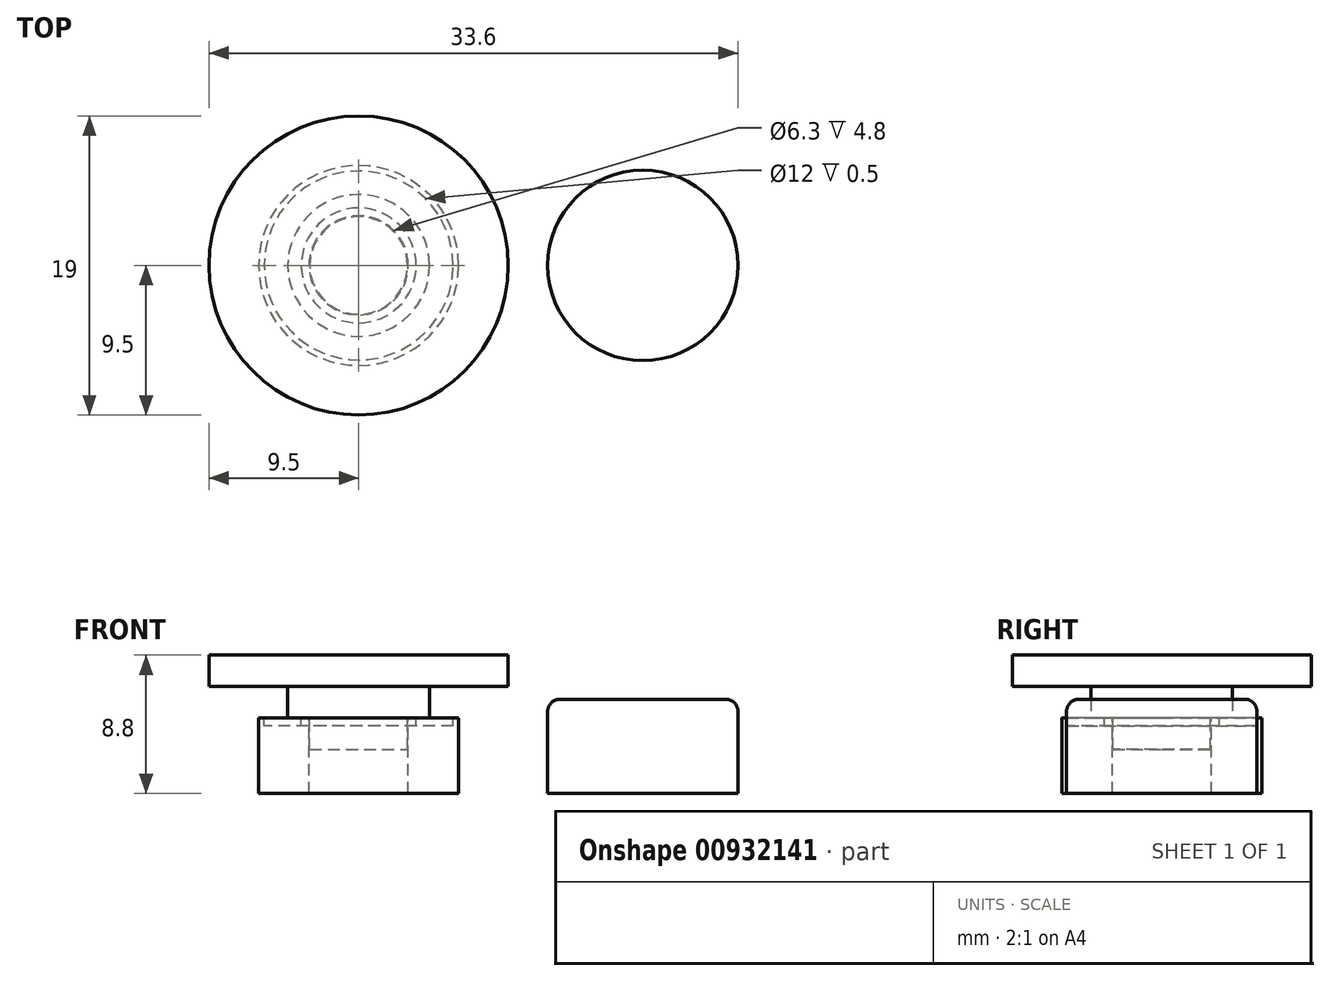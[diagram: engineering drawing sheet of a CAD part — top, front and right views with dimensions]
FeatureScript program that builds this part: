
annotation { "Feature Type Name" : "Feature", "Feature Type Description" : "" }
export const myFeature = defineFeature(function(context is Context, id is Id, definition is map)
    precondition{}
    {
        {
            var Q0;
            Q0=qCreatedBy(makeId("Top.planeOp"),FACE);
            var sketch = newSketch(context, id + "F0", { "sketchPlane" : qUnion([Q0])});
            skCircle(sketch, "E0", {"center": v(0, 0) * mm, "radius": 6.35 * mm});
            skSolve(sketch);
        }
        {
            var Q0;
            Q0=makeQuery(id+"F0.imprint","IMPRINT",FACE,{"disambiguationData":[TD([[makeQuery(id+"F0.imprint","IMPRINT",EDGE,{"derivedFrom":sQuery(id+"F0.wireOp",EDGE,"E0")}),1.0]])]});
            extrude(context, id + "F1", {"entities" : qUnion([Q0]), "depth" : 4.8 * mm, "offsetDistance" : 25 * mm});
        }
        {
            var Q0;
            Q0=makeQuery(id+"F1.opExtrude","CAP_FACE",FACE,{"disambiguationData":[OSD([sQuery(id+"F0.wireOp",EDGE,"E0")])],"isStart":false});
            var sketch = newSketch(context, id + "F2", { "sketchPlane" : qUnion([Q0])});
            skCircle(sketch, "E1", {"center": v(0, 0) * mm, "radius": 3.15 * mm});
            skSolve(sketch);
        }
        {
            var Q0;
            Q0=makeQuery(id+"F2.imprint","IMPRINT",FACE,{"disambiguationData":[TD([[makeQuery(id+"F2.imprint","IMPRINT",EDGE,{"derivedFrom":sQuery(id+"F2.wireOp",EDGE,"E1")}),1.0]])]});
            extrude(context, id + "F3", {"entities" : qUnion([Q0]), "operationType" : NewBodyOperationType.REMOVE, "endBound" : BoundingType.THROUGH_ALL, "oppositeDirection" : true, "depth" : 25 * mm, "offsetDistance" : 25 * mm});
        }
        {
            var Q0;
            Q0=qCreatedBy(makeId("Top.planeOp"),FACE);
            var sketch = newSketch(context, id + "F4", { "sketchPlane" : qUnion([Q0])});
            skLineSegment(sketch, "E2.bottom", {"start": v(22.5, 11.25) * mm, "end": v(-22.5, 11.25) * mm});
            skLineSegment(sketch, "E2.top", {"start": v(22.5, -11.25) * mm, "end": v(-22.5, -11.25) * mm});
            skLineSegment(sketch, "E2.left", {"start": v(27.5, 6.25) * mm, "end": v(27.5, -6.25) * mm});
            skLineSegment(sketch, "E2.right", {"start": v(-27.5, 6.25) * mm, "end": v(-27.5, -6.25) * mm});
            skPoint(sketch, "E2.middle", {"position": v(0, 0) * mm});
            skPoint(sketch, "E3.visualSharp", {"position": v(-27.5, 11.25) * mm});
            skArc(sketch, "E3.filletArc", {"start": v(-22.5, 11.25) * mm, "mid": v(-26.04, 9.79) * mm, "end": v(-27.5, 6.25) * mm});
            skPoint(sketch, "E4.visualSharp", {"position": v(-27.5, -11.25) * mm});
            skArc(sketch, "E4.filletArc", {"start": v(-27.5, -6.25) * mm, "mid": v(-26.04, -9.79) * mm, "end": v(-22.5, -11.25) * mm});
            skPoint(sketch, "E5.visualSharp", {"position": v(27.5, 11.25) * mm});
            skArc(sketch, "E5.filletArc", {"start": v(27.5, 6.25) * mm, "mid": v(26.04, 9.79) * mm, "end": v(22.5, 11.25) * mm});
            skPoint(sketch, "E6.visualSharp", {"position": v(27.5, -11.25) * mm});
            skArc(sketch, "E6.filletArc", {"start": v(22.5, -11.25) * mm, "mid": v(26.04, -9.79) * mm, "end": v(27.5, -6.25) * mm});
            skCircle(sketch, "E7", {"center": v(0, 0) * mm, "radius": 6.4 * mm});
            skSolve(sketch);
        }
        {
            var Q0;
            Q0=makeQuery(id+"F4.imprint","IMPRINT",FACE,{"disambiguationData":[TD([[makeQuery(id+"F4.imprint","IMPRINT",EDGE,{"derivedFrom":sQuery(id+"F4.wireOp",EDGE,"E2.bottom")}),1.0]])]});
            extrude(context, id + "F5", {"entities" : qUnion([Q0]), "depth" : 6 * mm, "offsetDistance" : 25 * mm});
        }
        {
            var Q0;
            Q0=makeQuery(id+"F1.opExtrude","CAP_FACE",FACE,{"disambiguationData":[OSD([sQuery(id+"F0.wireOp",EDGE,"E0")])],"isStart":false});
            var sketch = newSketch(context, id + "F6", { "sketchPlane" : qUnion([Q0])});
            skCircle(sketch, "E8", {"center": v(0, 0) * mm, "radius": 6 * mm});
            skCircle(sketch, "E9", {"center": v(0, 0) * mm, "radius": 3.65 * mm});
            skSolve(sketch);
        }
        {
            var Q0;
            Q0=makeQuery(id+"F6.imprint","IMPRINT",FACE,{"disambiguationData":[TD([[makeQuery(id+"F6.imprint","IMPRINT",EDGE,{"derivedFrom":sQuery(id+"F6.wireOp",EDGE,"E8")}),1.0]])]});
            extrude(context, id + "F7", {"entities" : qUnion([Q0]), "operationType" : NewBodyOperationType.REMOVE, "oppositeDirection" : true, "depth" : 0.5 * mm, "offsetDistance" : 25 * mm});
        }
        {
            var Q0;
            Q0=makeQuery(id+"F5.opExtrude","CAP_FACE",FACE,{"disambiguationData":[OSD([sQuery(id+"F4.wireOp",EDGE,"E2.bottom"),sQuery(id+"F4.wireOp",EDGE,"E2.top"),sQuery(id+"F4.wireOp",EDGE,"E2.left"),sQuery(id+"F4.wireOp",EDGE,"E2.right"),sQuery(id+"F4.wireOp",EDGE,"E3.filletArc"),sQuery(id+"F4.wireOp",EDGE,"E4.filletArc"),sQuery(id+"F4.wireOp",EDGE,"E5.filletArc"),sQuery(id+"F4.wireOp",EDGE,"E6.filletArc"),sQuery(id+"F4.wireOp",EDGE,"E7")])],"isStart":false});
            var sketch = newSketch(context, id + "F8", { "sketchPlane" : qUnion([Q0])});
            skLineSegment(sketch, "E10", {"start": v(0, 18.58) * mm, "end": v(0, -13.85) * mm, "construction": true});
            skCircle(sketch, "E11", {"center": v(-18.05, 0) * mm, "radius": 6.05 * mm});
            skCircle(sketch, "E12.MirrorC", {"center": v(18.05, 0) * mm, "radius": 6.05 * mm});
            skSolve(sketch);
        }
        {
            var Q0;
            Q0=makeQuery(id+"F8.imprint","IMPRINT",FACE,{"disambiguationData":[TD([[makeQuery(id+"F8.imprint","IMPRINT",EDGE,{"derivedFrom":sQuery(id+"F8.wireOp",EDGE,"E11")}),1.0]])]});
            var Q1;
            Q1=makeQuery(id+"F8.imprint","IMPRINT",FACE,{"disambiguationData":[TD([[makeQuery(id+"F8.imprint","IMPRINT",EDGE,{"derivedFrom":sQuery(id+"F8.wireOp",EDGE,"E12.MirrorC")}),-1.0]])]});
            extrude(context, id + "F9", {"entities" : qUnion([Q0, Q1]), "operationType" : NewBodyOperationType.REMOVE, "endBound" : BoundingType.THROUGH_ALL, "oppositeDirection" : true, "depth" : 25 * mm, "offsetDistance" : 25 * mm});
        }
        {
            var Q0;
            Q0=makeQuery(id+"F5.opExtrude","CAP_FACE",FACE,{"disambiguationData":[OSD([sQuery(id+"F4.wireOp",EDGE,"E2.bottom"),sQuery(id+"F4.wireOp",EDGE,"E2.top"),sQuery(id+"F4.wireOp",EDGE,"E2.left"),sQuery(id+"F4.wireOp",EDGE,"E2.right"),sQuery(id+"F4.wireOp",EDGE,"E3.filletArc"),sQuery(id+"F4.wireOp",EDGE,"E4.filletArc"),sQuery(id+"F4.wireOp",EDGE,"E5.filletArc"),sQuery(id+"F4.wireOp",EDGE,"E6.filletArc"),sQuery(id+"F4.wireOp",EDGE,"E7")])],"isStart":false});
            fillet(context, id + "F10", {"entities" : qUnion([Q0]), "radius" : 0.8 * mm, "tangentPropagation" : true, "allowEdgeOverflow" : false});
        }
        {
            var Q0;
            Q0=makeQuery(id+"F7.boolean.opBoolean","SPLIT",FACE,{"disambiguationData":[TD([makeQuery(id+"F3.boolean.opBoolean","COPY",FACE,{"derivedFrom":makeQuery(id+"F3.opExtrude","SWEPT_FACE",FACE,{"disambiguationData":[OSD([sQuery(id+"F2.wireOp",EDGE,"E1")])]})})])],"derivedFrom":makeQuery(id+"F1.opExtrude","CAP_FACE",FACE,{"disambiguationData":[OSD([sQuery(id+"F0.wireOp",EDGE,"E0")])],"isStart":false})});
            cPlane(context, id + "F11", {"entities" : qUnion([Q0]), "cplaneType" : CPlaneType.OFFSET, "offset" : 0 * mm, "width" : 150 * mm, "height" : 150 * mm});
        }
        {
            var Q0;
            Q0=qCreatedBy(id+"F11.planeOp",FACE);
            var sketch = newSketch(context, id + "F12", { "sketchPlane" : qUnion([Q0])});
            skCircle(sketch, "E13", {"center": v(0, 0) * mm, "radius": 4.5 * mm});
            skSolve(sketch);
        }
        {
            var Q0;
            Q0 = qSketchRegion(id + "F12", true);
            extrude(context, id + "F13", {"entities" : qUnion([Q0]), "depth" : 2 * mm, "offsetDistance" : 25 * mm});
        }
        {
            var Q0;
            Q0=makeQuery(id+"F13.opExtrude","CAP_FACE",FACE,{"disambiguationData":[OSD([sQuery(id+"F12.wireOp",EDGE,"E13")])],"isStart":false});
            var sketch = newSketch(context, id + "F14", { "sketchPlane" : qUnion([Q0])});
            skCircle(sketch, "E14", {"center": v(0, 0) * mm, "radius": 9.5 * mm});
            skSolve(sketch);
        }
        {
            var Q0;
            Q0=makeQuery(id+"F14.imprint","IMPRINT",FACE,{"disambiguationData":[TD([[makeQuery(id+"F14.imprint","IMPRINT",EDGE,{"derivedFrom":makeQuery(id+"F13.opExtrude","CAP_EDGE",EDGE,{"disambiguationData":[OSD([sQuery(id+"F12.wireOp",EDGE,"E13")])],"isStart":false})}),1.0]])]});
            var Q1;
            Q1=makeQuery(id+"F14.imprint","IMPRINT",FACE,{"disambiguationData":[TD([[makeQuery(id+"F14.imprint","IMPRINT",EDGE,{"derivedFrom":sQuery(id+"F14.wireOp",EDGE,"E14")}),1.0]])]});
            extrude(context, id + "F15", {"entities" : qUnion([Q0, Q1]), "operationType" : NewBodyOperationType.ADD, "depth" : 2 * mm, "offsetDistance" : 25 * mm});
        }
        {
            var Q0;
            Q0=makeQuery(id+"F13.opExtrude","CAP_FACE",FACE,{"disambiguationData":[OSD([sQuery(id+"F12.wireOp",EDGE,"E13")])],"isStart":true});
            var sketch = newSketch(context, id + "F16", { "sketchPlane" : qUnion([Q0])});
            skCircle(sketch, "E15", {"center": v(0, 0) * mm, "radius": 3.1 * mm});
            skSolve(sketch);
        }
        {
            var Q0;
            Q0=makeQuery(id+"F16.imprint","IMPRINT",FACE,{"disambiguationData":[TD([[makeQuery(id+"F16.imprint","IMPRINT",EDGE,{"derivedFrom":sQuery(id+"F16.wireOp",EDGE,"E15")}),1.0]])]});
            extrude(context, id + "F17", {"entities" : qUnion([Q0]), "operationType" : NewBodyOperationType.ADD, "depth" : 2 * mm, "offsetDistance" : 25 * mm});
        }
    });
